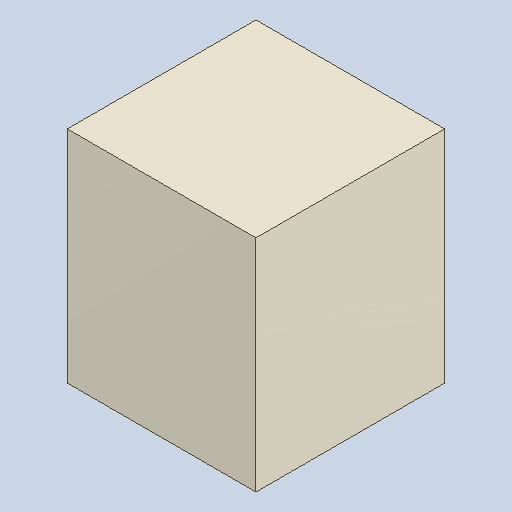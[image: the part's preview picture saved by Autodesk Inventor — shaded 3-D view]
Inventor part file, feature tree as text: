
AUTODESK INVENTOR PART (.ipt)
format: ipt  version: 2023.4 (Build 274418000, 418)  size: 82,944 bytes
history: native  units: mm
features: extrude x1
ambient origin geometry x8: Origin, YZ Plane, XZ Plane, XY Plane, X Axis, Y Axis, Z Axis, Center Point
bodies: Solid1 (feature_tree)
feature tree (1):
  extrude  "Extruded_24"  [1 undecoded]
note: 1 required parameter value undecoded (feature->parameter linkage not recoverable at this tier; creation-order binding heuristic only, values carry confidence <= 0.55)
